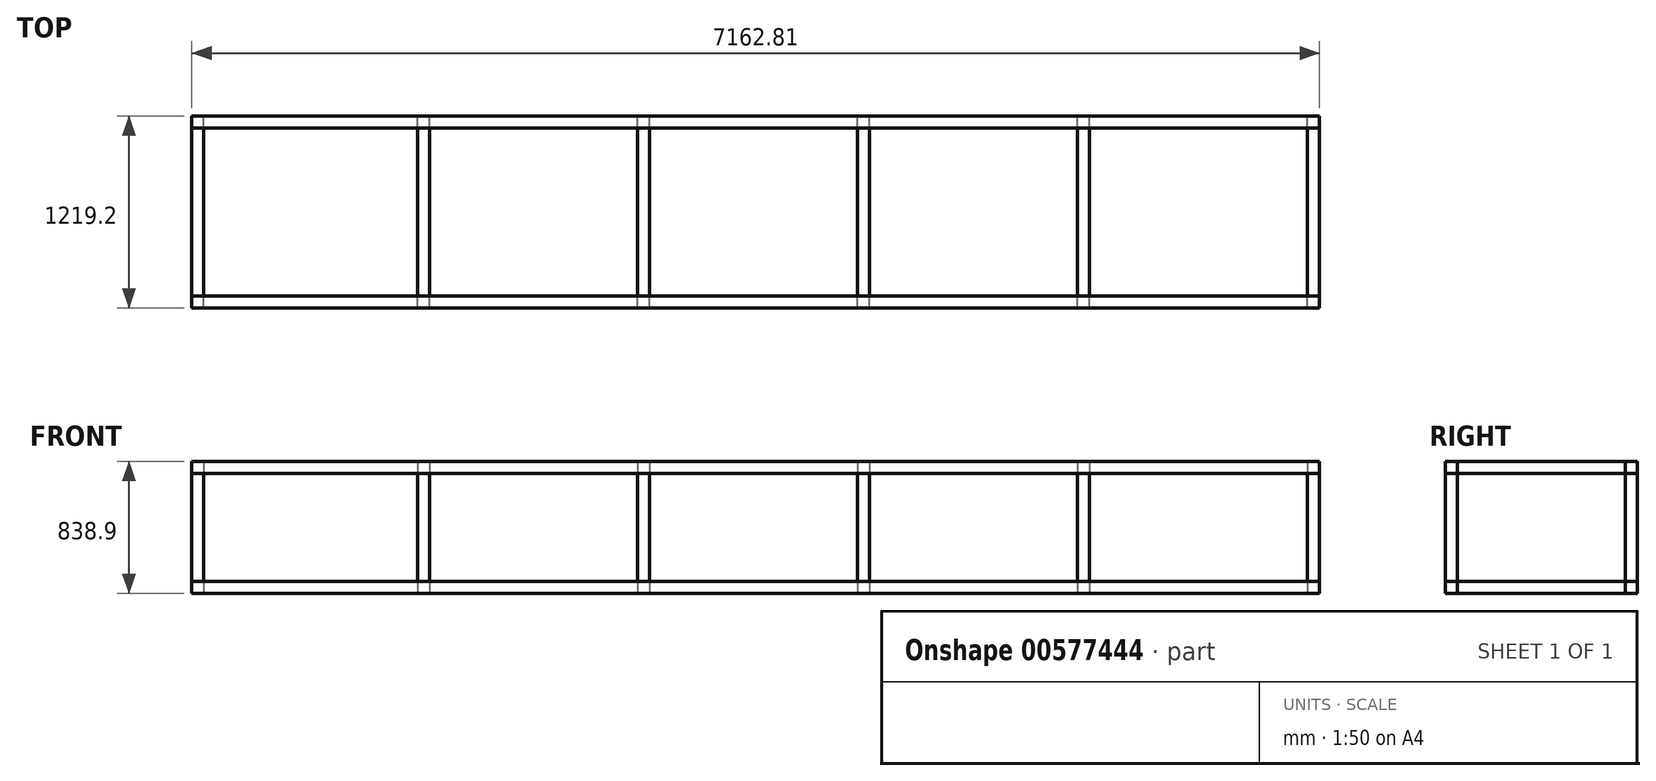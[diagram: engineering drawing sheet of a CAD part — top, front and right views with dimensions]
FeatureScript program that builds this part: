
annotation { "Feature Type Name" : "Feature", "Feature Type Description" : "" }
export const myFeature = defineFeature(function(context is Context, id is Id, definition is map)
    precondition{}
    {
        {
            var Q0;
            Q0=qCreatedBy(makeId("Front.planeOp"),FACE);
            var sketch = newSketch(context, id + "F0", { "sketchPlane" : qUnion([Q0])});
            skLineSegment(sketch, "E0.bottom", {"start": v(-3581.4, 38.1) * mm, "end": v(3581.4, 38.1) * mm});
            skLineSegment(sketch, "E0.top", {"start": v(-3581.4, -38.1) * mm, "end": v(3581.4, -38.1) * mm});
            skLineSegment(sketch, "E0.left", {"start": v(-3581.4, 38.1) * mm, "end": v(-3581.4, -38.1) * mm});
            skLineSegment(sketch, "E0.right", {"start": v(3581.4, 38.1) * mm, "end": v(3581.4, -38.1) * mm});
            skPoint(sketch, "E0.middle", {"position": v(0, 0) * mm});
            skSolve(sketch);
        }
        {
            var Q0;
            Q0=makeQuery(id+"F0.imprint","IMPRINT",FACE,{"disambiguationData":[TD([[makeQuery(id+"F0.imprint","IMPRINT",EDGE,{"derivedFrom":sQuery(id+"F0.wireOp",EDGE,"E0.bottom")}),-1.0]])]});
            extrude(context, id + "F1", {"entities" : qUnion([Q0]), "depth" : 76.2 * mm, "offsetDistance" : 25.4 * mm});
        }
        {
            var Q0;
            Q0=qCreatedBy(makeId("Front.planeOp"),FACE);
            var sketch = newSketch(context, id + "F2", { "sketchPlane" : qUnion([Q0])});
            skLineSegment(sketch, "E1.bottom", {"start": v(3581.4, 800.8) * mm, "end": v(-3581.4, 800.8) * mm});
            skLineSegment(sketch, "E1.top", {"start": v(3581.4, 724.6) * mm, "end": v(-3581.4, 724.6) * mm});
            skLineSegment(sketch, "E1.left", {"start": v(3581.4, 800.8) * mm, "end": v(3581.4, 724.6) * mm});
            skLineSegment(sketch, "E1.right", {"start": v(-3581.4, 800.8) * mm, "end": v(-3581.4, 724.6) * mm});
            skPoint(sketch, "E1.middle", {"position": v(0, 762.7) * mm});
            skSolve(sketch);
        }
        {
            var Q0;
            Q0=makeQuery(id+"F2.imprint","IMPRINT",FACE,{"disambiguationData":[TD([[makeQuery(id+"F2.imprint","IMPRINT",EDGE,{"derivedFrom":sQuery(id+"F2.wireOp",EDGE,"E1.bottom")}),1.0]])]});
            extrude(context, id + "F3", {"entities" : qUnion([Q0]), "depth" : 76.2 * mm, "offsetDistance" : 25.4 * mm});
        }
        {
            var Q0;
            Q0=qCreatedBy(makeId("Front.planeOp"),FACE);
            var sketch = newSketch(context, id + "F4", { "sketchPlane" : qUnion([Q0])});
            skLineSegment(sketch, "E2.bottom", {"start": v(-3505.19, 723.93) * mm, "end": v(-3581.39, 723.93) * mm});
            skLineSegment(sketch, "E2.top", {"start": v(-3505.19, 38.13) * mm, "end": v(-3581.39, 38.13) * mm});
            skLineSegment(sketch, "E2.left", {"start": v(-3505.19, 723.93) * mm, "end": v(-3505.19, 38.13) * mm});
            skLineSegment(sketch, "E2.right", {"start": v(-3581.39, 723.93) * mm, "end": v(-3581.39, 38.13) * mm});
            skPoint(sketch, "E2.middle", {"position": v(-3543.29, 381.03) * mm});
            skSolve(sketch);
        }
        {
            var Q0;
            Q0=makeQuery(id+"F4.imprint","IMPRINT",FACE,{"disambiguationData":[TD([[makeQuery(id+"F4.imprint","IMPRINT",EDGE,{"derivedFrom":sQuery(id+"F4.wireOp",EDGE,"E2.bottom")}),1.0]])]});
            extrude(context, id + "F5", {"entities" : qUnion([Q0]), "depth" : 76.2 * mm, "offsetDistance" : 25.4 * mm});
        }
        {
            var Q0;
            Q0=makeQuery(id+"F5.opExtrude","SWEPT_BODY",BODY,{"disambiguationData":[OSD([sQuery(id+"F4.wireOp",EDGE,"E2.bottom"),sQuery(id+"F4.wireOp",EDGE,"E2.top"),sQuery(id+"F4.wireOp",EDGE,"E2.left"),sQuery(id+"F4.wireOp",EDGE,"E2.right")])]});
            var Q1;
            Q1=qCreatedBy(makeId("Right.planeOp"),FACE);
            transform(context, id + "F6", {"entities" : qUnion([Q0]), "transformType" : TransformType.TRANSLATION_DISTANCE, "transformDirection" : qUnion([Q1]), "distance" : 1435.1 * mm, "makeCopy" : true});
        }
        {
            var Q0;
            Q0=makeQuery(id+"F6.opPattern","COPY",BODY,{"derivedFrom":makeQuery(id+"F5.opExtrude","SWEPT_BODY",BODY,{"disambiguationData":[OSD([sQuery(id+"F4.wireOp",EDGE,"E2.bottom"),sQuery(id+"F4.wireOp",EDGE,"E2.top"),sQuery(id+"F4.wireOp",EDGE,"E2.left"),sQuery(id+"F4.wireOp",EDGE,"E2.right")])]}),"instanceName":"1"});
            var Q1;
            Q1=qCreatedBy(makeId("Right.planeOp"),FACE);
            transform(context, id + "F7", {"entities" : qUnion([Q0]), "transformType" : TransformType.TRANSLATION_DISTANCE, "transformDirection" : qUnion([Q1]), "distance" : 1397 * mm, "makeCopy" : true});
        }
        {
            var Q0;
            Q0=makeQuery(id+"F7.opPattern","COPY",BODY,{"derivedFrom":makeQuery(id+"F6.opPattern","COPY",BODY,{"derivedFrom":makeQuery(id+"F5.opExtrude","SWEPT_BODY",BODY,{"disambiguationData":[OSD([sQuery(id+"F4.wireOp",EDGE,"E2.bottom"),sQuery(id+"F4.wireOp",EDGE,"E2.top"),sQuery(id+"F4.wireOp",EDGE,"E2.left"),sQuery(id+"F4.wireOp",EDGE,"E2.right")])]}),"instanceName":"1"}),"instanceName":"1"});
            var Q1;
            Q1=qCreatedBy(makeId("Right.planeOp"),FACE);
            transform(context, id + "F8", {"entities" : qUnion([Q0]), "transformType" : TransformType.TRANSLATION_DISTANCE, "transformDirection" : qUnion([Q1]), "distance" : 1397 * mm, "makeCopy" : true});
        }
        {
            var Q0;
            Q0=makeQuery(id+"F8.opPattern","COPY",BODY,{"derivedFrom":makeQuery(id+"F7.opPattern","COPY",BODY,{"derivedFrom":makeQuery(id+"F6.opPattern","COPY",BODY,{"derivedFrom":makeQuery(id+"F5.opExtrude","SWEPT_BODY",BODY,{"disambiguationData":[OSD([sQuery(id+"F4.wireOp",EDGE,"E2.bottom"),sQuery(id+"F4.wireOp",EDGE,"E2.top"),sQuery(id+"F4.wireOp",EDGE,"E2.left"),sQuery(id+"F4.wireOp",EDGE,"E2.right")])]}),"instanceName":"1"}),"instanceName":"1"}),"instanceName":"1"});
            var Q1;
            Q1=qCreatedBy(makeId("Right.planeOp"),FACE);
            transform(context, id + "F9", {"entities" : qUnion([Q0]), "transformType" : TransformType.TRANSLATION_DISTANCE, "transformDirection" : qUnion([Q1]), "distance" : 1397 * mm, "makeCopy" : true});
        }
        {
            var Q0;
            Q0=makeQuery(id+"F9.opPattern","COPY",BODY,{"derivedFrom":makeQuery(id+"F8.opPattern","COPY",BODY,{"derivedFrom":makeQuery(id+"F7.opPattern","COPY",BODY,{"derivedFrom":makeQuery(id+"F6.opPattern","COPY",BODY,{"derivedFrom":makeQuery(id+"F5.opExtrude","SWEPT_BODY",BODY,{"disambiguationData":[OSD([sQuery(id+"F4.wireOp",EDGE,"E2.bottom"),sQuery(id+"F4.wireOp",EDGE,"E2.top"),sQuery(id+"F4.wireOp",EDGE,"E2.left"),sQuery(id+"F4.wireOp",EDGE,"E2.right")])]}),"instanceName":"1"}),"instanceName":"1"}),"instanceName":"1"}),"instanceName":"1"});
            var Q1;
            Q1=qCreatedBy(makeId("Right.planeOp"),FACE);
            transform(context, id + "F10", {"entities" : qUnion([Q0]), "transformType" : TransformType.TRANSLATION_DISTANCE, "transformDirection" : qUnion([Q1]), "distance" : 1460.5 * mm, "makeCopy" : true});
        }
        {
            var Q0;
            Q0=makeQuery(id+"F9.opPattern","COPY",BODY,{"derivedFrom":makeQuery(id+"F8.opPattern","COPY",BODY,{"derivedFrom":makeQuery(id+"F7.opPattern","COPY",BODY,{"derivedFrom":makeQuery(id+"F6.opPattern","COPY",BODY,{"derivedFrom":makeQuery(id+"F5.opExtrude","SWEPT_BODY",BODY,{"disambiguationData":[OSD([sQuery(id+"F4.wireOp",EDGE,"E2.bottom"),sQuery(id+"F4.wireOp",EDGE,"E2.top"),sQuery(id+"F4.wireOp",EDGE,"E2.left"),sQuery(id+"F4.wireOp",EDGE,"E2.right")])]}),"instanceName":"1"}),"instanceName":"1"}),"instanceName":"1"}),"instanceName":"1"});
            var Q1;
            Q1=makeQuery(id+"F8.opPattern","COPY",BODY,{"derivedFrom":makeQuery(id+"F7.opPattern","COPY",BODY,{"derivedFrom":makeQuery(id+"F6.opPattern","COPY",BODY,{"derivedFrom":makeQuery(id+"F5.opExtrude","SWEPT_BODY",BODY,{"disambiguationData":[OSD([sQuery(id+"F4.wireOp",EDGE,"E2.bottom"),sQuery(id+"F4.wireOp",EDGE,"E2.top"),sQuery(id+"F4.wireOp",EDGE,"E2.left"),sQuery(id+"F4.wireOp",EDGE,"E2.right")])]}),"instanceName":"1"}),"instanceName":"1"}),"instanceName":"1"});
            var Q2;
            Q2=makeQuery(id+"F3.opExtrude","SWEPT_BODY",BODY,{"disambiguationData":[OSD([sQuery(id+"F2.wireOp",EDGE,"E1.bottom"),sQuery(id+"F2.wireOp",EDGE,"E1.top"),sQuery(id+"F2.wireOp",EDGE,"E1.left"),sQuery(id+"F2.wireOp",EDGE,"E1.right")])]});
            var Q3;
            Q3=makeQuery(id+"F5.opExtrude","SWEPT_BODY",BODY,{"disambiguationData":[OSD([sQuery(id+"F4.wireOp",EDGE,"E2.bottom"),sQuery(id+"F4.wireOp",EDGE,"E2.top"),sQuery(id+"F4.wireOp",EDGE,"E2.left"),sQuery(id+"F4.wireOp",EDGE,"E2.right")])]});
            var Q4;
            Q4=makeQuery(id+"F1.opExtrude","SWEPT_BODY",BODY,{"disambiguationData":[OSD([sQuery(id+"F0.wireOp",EDGE,"E0.bottom"),sQuery(id+"F0.wireOp",EDGE,"E0.top"),sQuery(id+"F0.wireOp",EDGE,"E0.left"),sQuery(id+"F0.wireOp",EDGE,"E0.right")])]});
            var Q5;
            Q5=makeQuery(id+"F7.opPattern","COPY",BODY,{"derivedFrom":makeQuery(id+"F6.opPattern","COPY",BODY,{"derivedFrom":makeQuery(id+"F5.opExtrude","SWEPT_BODY",BODY,{"disambiguationData":[OSD([sQuery(id+"F4.wireOp",EDGE,"E2.bottom"),sQuery(id+"F4.wireOp",EDGE,"E2.top"),sQuery(id+"F4.wireOp",EDGE,"E2.left"),sQuery(id+"F4.wireOp",EDGE,"E2.right")])]}),"instanceName":"1"}),"instanceName":"1"});
            var Q6;
            Q6=makeQuery(id+"F6.opPattern","COPY",BODY,{"derivedFrom":makeQuery(id+"F5.opExtrude","SWEPT_BODY",BODY,{"disambiguationData":[OSD([sQuery(id+"F4.wireOp",EDGE,"E2.bottom"),sQuery(id+"F4.wireOp",EDGE,"E2.top"),sQuery(id+"F4.wireOp",EDGE,"E2.left"),sQuery(id+"F4.wireOp",EDGE,"E2.right")])]}),"instanceName":"1"});
            var Q7;
            Q7=makeQuery(id+"F10.opPattern","COPY",BODY,{"derivedFrom":makeQuery(id+"F9.opPattern","COPY",BODY,{"derivedFrom":makeQuery(id+"F8.opPattern","COPY",BODY,{"derivedFrom":makeQuery(id+"F7.opPattern","COPY",BODY,{"derivedFrom":makeQuery(id+"F6.opPattern","COPY",BODY,{"derivedFrom":makeQuery(id+"F5.opExtrude","SWEPT_BODY",BODY,{"disambiguationData":[OSD([sQuery(id+"F4.wireOp",EDGE,"E2.bottom"),sQuery(id+"F4.wireOp",EDGE,"E2.top"),sQuery(id+"F4.wireOp",EDGE,"E2.left"),sQuery(id+"F4.wireOp",EDGE,"E2.right")])]}),"instanceName":"1"}),"instanceName":"1"}),"instanceName":"1"}),"instanceName":"1"}),"instanceName":"1"});
            var Q8;
            Q8=qCreatedBy(makeId("Front.planeOp"),FACE);
            transform(context, id + "F11", {"entities" : qUnion([Q0, Q1, Q2, Q3, Q4, Q5, Q6, Q7]), "transformType" : TransformType.TRANSLATION_DISTANCE, "transformDirection" : qUnion([Q8]), "distance" : 1143 * mm, "oppositeDirection" : true, "makeCopy" : true});
        }
        {
            var Q0;
            Q0=makeQuery(id+"F1.opExtrude","SWEPT_FACE",FACE,{"disambiguationData":[OSD([sQuery(id+"F0.wireOp",EDGE,"E0.right")])]});
            var sketch = newSketch(context, id + "F12", { "sketchPlane" : qUnion([Q0])});
            skLineSegment(sketch, "E3.bottom", {"start": v(1066.8, 38.1) * mm, "end": v(0, 38.1) * mm});
            skLineSegment(sketch, "E3.top", {"start": v(1066.8, -38.1) * mm, "end": v(0, -38.1) * mm});
            skLineSegment(sketch, "E3.left", {"start": v(1066.8, 38.1) * mm, "end": v(1066.8, -38.1) * mm});
            skLineSegment(sketch, "E3.right", {"start": v(0, 38.1) * mm, "end": v(0, -38.1) * mm});
            skPoint(sketch, "E3.middle", {"position": v(533.4, 0) * mm});
            skSolve(sketch);
        }
        {
            var Q0;
            Q0=makeQuery(id+"F12.imprint","IMPRINT",FACE,{"disambiguationData":[TD([[makeQuery(id+"F12.imprint","IMPRINT",EDGE,{"derivedFrom":sQuery(id+"F12.wireOp",EDGE,"E3.bottom")}),1.0]])]});
            extrude(context, id + "F13", {"entities" : qUnion([Q0]), "oppositeDirection" : true, "depth" : 76.2 * mm, "offsetDistance" : 25.4 * mm});
        }
        {
            var Q0;
            Q0=makeQuery(id+"F13.opExtrude","SWEPT_BODY",BODY,{"disambiguationData":[OSD([sQuery(id+"F12.wireOp",EDGE,"E3.bottom"),sQuery(id+"F12.wireOp",EDGE,"E3.top"),sQuery(id+"F12.wireOp",EDGE,"E3.left"),sQuery(id+"F12.wireOp",EDGE,"E3.right")])]});
            var Q1;
            Q1=qCreatedBy(makeId("Right.planeOp"),FACE);
            transform(context, id + "F14", {"entities" : qUnion([Q0]), "transformType" : TransformType.TRANSLATION_DISTANCE, "transformDirection" : qUnion([Q1]), "distance" : 7086.6 * mm, "oppositeDirection" : true, "makeCopy" : true});
        }
        {
            var Q0;
            Q0=makeQuery(id+"F14.opPattern","COPY",BODY,{"derivedFrom":makeQuery(id+"F13.opExtrude","SWEPT_BODY",BODY,{"disambiguationData":[OSD([sQuery(id+"F12.wireOp",EDGE,"E3.bottom"),sQuery(id+"F12.wireOp",EDGE,"E3.top"),sQuery(id+"F12.wireOp",EDGE,"E3.left"),sQuery(id+"F12.wireOp",EDGE,"E3.right")])]}),"instanceName":"1"});
            var Q1;
            Q1=qCreatedBy(makeId("Right.planeOp"),FACE);
            transform(context, id + "F15", {"entities" : qUnion([Q0]), "transformType" : TransformType.TRANSLATION_DISTANCE, "transformDirection" : qUnion([Q1]), "distance" : 1435.1 * mm, "makeCopy" : true});
        }
        {
            var Q0;
            Q0=makeQuery(id+"F15.opPattern","COPY",BODY,{"derivedFrom":makeQuery(id+"F14.opPattern","COPY",BODY,{"derivedFrom":makeQuery(id+"F13.opExtrude","SWEPT_BODY",BODY,{"disambiguationData":[OSD([sQuery(id+"F12.wireOp",EDGE,"E3.bottom"),sQuery(id+"F12.wireOp",EDGE,"E3.top"),sQuery(id+"F12.wireOp",EDGE,"E3.left"),sQuery(id+"F12.wireOp",EDGE,"E3.right")])]}),"instanceName":"1"}),"instanceName":"1"});
            var Q1;
            Q1=qCreatedBy(makeId("Right.planeOp"),FACE);
            transform(context, id + "F16", {"entities" : qUnion([Q0]), "transformType" : TransformType.TRANSLATION_DISTANCE, "transformDirection" : qUnion([Q1]), "distance" : 1397 * mm, "makeCopy" : true});
        }
        {
            var Q0;
            Q0=makeQuery(id+"F16.opPattern","COPY",BODY,{"derivedFrom":makeQuery(id+"F15.opPattern","COPY",BODY,{"derivedFrom":makeQuery(id+"F14.opPattern","COPY",BODY,{"derivedFrom":makeQuery(id+"F13.opExtrude","SWEPT_BODY",BODY,{"disambiguationData":[OSD([sQuery(id+"F12.wireOp",EDGE,"E3.bottom"),sQuery(id+"F12.wireOp",EDGE,"E3.top"),sQuery(id+"F12.wireOp",EDGE,"E3.left"),sQuery(id+"F12.wireOp",EDGE,"E3.right")])]}),"instanceName":"1"}),"instanceName":"1"}),"instanceName":"1"});
            var Q1;
            Q1=qCreatedBy(makeId("Right.planeOp"),FACE);
            transform(context, id + "F17", {"entities" : qUnion([Q0]), "transformType" : TransformType.TRANSLATION_DISTANCE, "transformDirection" : qUnion([Q1]), "distance" : 1397 * mm, "makeCopy" : true});
        }
        {
            var Q0;
            Q0=makeQuery(id+"F17.opPattern","COPY",BODY,{"derivedFrom":makeQuery(id+"F16.opPattern","COPY",BODY,{"derivedFrom":makeQuery(id+"F15.opPattern","COPY",BODY,{"derivedFrom":makeQuery(id+"F14.opPattern","COPY",BODY,{"derivedFrom":makeQuery(id+"F13.opExtrude","SWEPT_BODY",BODY,{"disambiguationData":[OSD([sQuery(id+"F12.wireOp",EDGE,"E3.bottom"),sQuery(id+"F12.wireOp",EDGE,"E3.top"),sQuery(id+"F12.wireOp",EDGE,"E3.left"),sQuery(id+"F12.wireOp",EDGE,"E3.right")])]}),"instanceName":"1"}),"instanceName":"1"}),"instanceName":"1"}),"instanceName":"1"});
            var Q1;
            Q1=qCreatedBy(makeId("Right.planeOp"),FACE);
            transform(context, id + "F18", {"entities" : qUnion([Q0]), "transformType" : TransformType.TRANSLATION_DISTANCE, "transformDirection" : qUnion([Q1]), "distance" : 1397 * mm, "makeCopy" : true});
        }
        {
            var Q0;
            Q0=makeQuery(id+"F16.opPattern","COPY",BODY,{"derivedFrom":makeQuery(id+"F15.opPattern","COPY",BODY,{"derivedFrom":makeQuery(id+"F14.opPattern","COPY",BODY,{"derivedFrom":makeQuery(id+"F13.opExtrude","SWEPT_BODY",BODY,{"disambiguationData":[OSD([sQuery(id+"F12.wireOp",EDGE,"E3.bottom"),sQuery(id+"F12.wireOp",EDGE,"E3.top"),sQuery(id+"F12.wireOp",EDGE,"E3.left"),sQuery(id+"F12.wireOp",EDGE,"E3.right")])]}),"instanceName":"1"}),"instanceName":"1"}),"instanceName":"1"});
            var Q1;
            Q1=makeQuery(id+"F18.opPattern","COPY",BODY,{"derivedFrom":makeQuery(id+"F17.opPattern","COPY",BODY,{"derivedFrom":makeQuery(id+"F16.opPattern","COPY",BODY,{"derivedFrom":makeQuery(id+"F15.opPattern","COPY",BODY,{"derivedFrom":makeQuery(id+"F14.opPattern","COPY",BODY,{"derivedFrom":makeQuery(id+"F13.opExtrude","SWEPT_BODY",BODY,{"disambiguationData":[OSD([sQuery(id+"F12.wireOp",EDGE,"E3.bottom"),sQuery(id+"F12.wireOp",EDGE,"E3.top"),sQuery(id+"F12.wireOp",EDGE,"E3.left"),sQuery(id+"F12.wireOp",EDGE,"E3.right")])]}),"instanceName":"1"}),"instanceName":"1"}),"instanceName":"1"}),"instanceName":"1"}),"instanceName":"1"});
            var Q2;
            Q2=makeQuery(id+"F14.opPattern","COPY",BODY,{"derivedFrom":makeQuery(id+"F13.opExtrude","SWEPT_BODY",BODY,{"disambiguationData":[OSD([sQuery(id+"F12.wireOp",EDGE,"E3.bottom"),sQuery(id+"F12.wireOp",EDGE,"E3.top"),sQuery(id+"F12.wireOp",EDGE,"E3.left"),sQuery(id+"F12.wireOp",EDGE,"E3.right")])]}),"instanceName":"1"});
            var Q3;
            Q3=makeQuery(id+"F15.opPattern","COPY",BODY,{"derivedFrom":makeQuery(id+"F14.opPattern","COPY",BODY,{"derivedFrom":makeQuery(id+"F13.opExtrude","SWEPT_BODY",BODY,{"disambiguationData":[OSD([sQuery(id+"F12.wireOp",EDGE,"E3.bottom"),sQuery(id+"F12.wireOp",EDGE,"E3.top"),sQuery(id+"F12.wireOp",EDGE,"E3.left"),sQuery(id+"F12.wireOp",EDGE,"E3.right")])]}),"instanceName":"1"}),"instanceName":"1"});
            var Q4;
            Q4=makeQuery(id+"F13.opExtrude","SWEPT_BODY",BODY,{"disambiguationData":[OSD([sQuery(id+"F12.wireOp",EDGE,"E3.bottom"),sQuery(id+"F12.wireOp",EDGE,"E3.top"),sQuery(id+"F12.wireOp",EDGE,"E3.left"),sQuery(id+"F12.wireOp",EDGE,"E3.right")])]});
            var Q5;
            Q5=makeQuery(id+"F17.opPattern","COPY",BODY,{"derivedFrom":makeQuery(id+"F16.opPattern","COPY",BODY,{"derivedFrom":makeQuery(id+"F15.opPattern","COPY",BODY,{"derivedFrom":makeQuery(id+"F14.opPattern","COPY",BODY,{"derivedFrom":makeQuery(id+"F13.opExtrude","SWEPT_BODY",BODY,{"disambiguationData":[OSD([sQuery(id+"F12.wireOp",EDGE,"E3.bottom"),sQuery(id+"F12.wireOp",EDGE,"E3.top"),sQuery(id+"F12.wireOp",EDGE,"E3.left"),sQuery(id+"F12.wireOp",EDGE,"E3.right")])]}),"instanceName":"1"}),"instanceName":"1"}),"instanceName":"1"}),"instanceName":"1"});
            var Q6;
            Q6=qCreatedBy(makeId("Top.planeOp"),FACE);
            transform(context, id + "F19", {"entities" : qUnion([Q0, Q1, Q2, Q3, Q4, Q5]), "transformType" : TransformType.TRANSLATION_DISTANCE, "transformDirection" : qUnion([Q6]), "distance" : 762 * mm, "makeCopy" : true});
        }
    });
